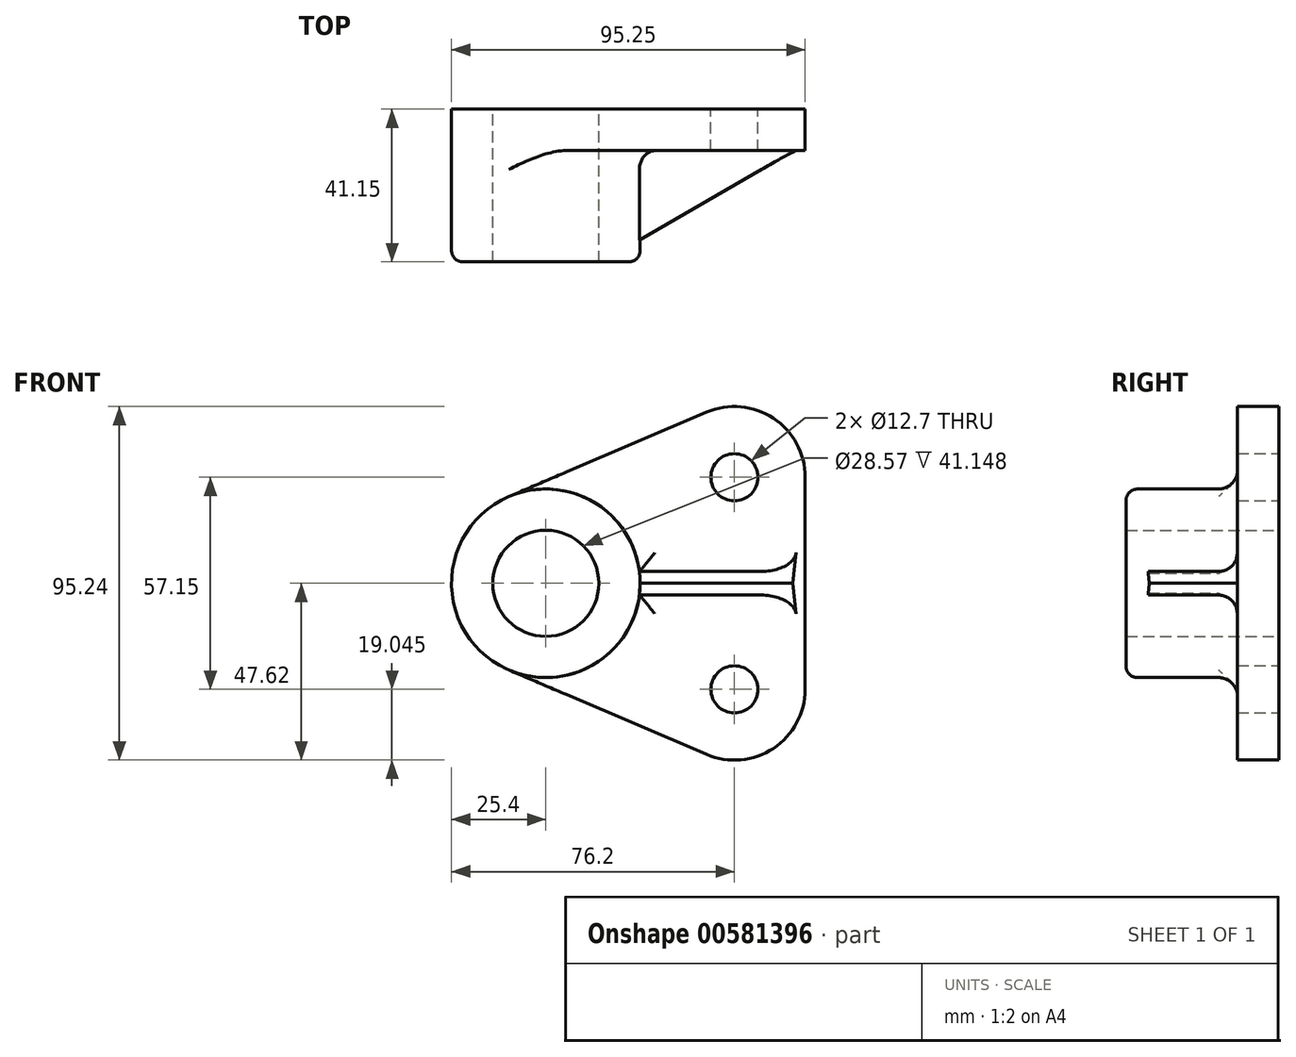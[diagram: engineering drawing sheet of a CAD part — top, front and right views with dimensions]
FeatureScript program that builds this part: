
annotation { "Feature Type Name" : "Feature", "Feature Type Description" : "" }
export const myFeature = defineFeature(function(context is Context, id is Id, definition is map)
    precondition{}
    {
        {
            var Q0;
            Q0=qCreatedBy(makeId("Front.planeOp"),FACE);
            var sketch = newSketch(context, id + "F0", { "sketchPlane" : qUnion([Q0])});
            skCircle(sketch, "E0", {"center": v(0, 0) * mm, "radius": 25.4 * mm});
            skCircle(sketch, "E1", {"center": v(0, 0) * mm, "radius": 14.29 * mm});
            skLineSegment(sketch, "E2", {"start": v(0, 0) * mm, "end": v(69.85, 0) * mm, "construction": true});
            skLineSegment(sketch, "E3", {"start": v(-9.97, 23.36) * mm, "end": v(43.33, 46.1) * mm});
            skLineSegment(sketch, "E4", {"start": v(69.85, 28.58) * mm, "end": v(69.85, 0) * mm});
            skPoint(sketch, "E5.visualSharp", {"position": v(69.85, 57.41) * mm});
            skArc(sketch, "E5.filletArc", {"start": v(69.85, 28.58) * mm, "mid": v(61.3, 44.47) * mm, "end": v(43.33, 46.1) * mm});
            skLineSegment(sketch, "E6.MirrorCS", {"start": v(69.85, -28.58) * mm, "end": v(69.85, 0) * mm});
            skArc(sketch, "E7.MirrorCS", {"start": v(69.85, -28.58) * mm, "mid": v(61.3, -44.47) * mm, "end": v(43.33, -46.1) * mm});
            skLineSegment(sketch, "E8.MirrorCS", {"start": v(-9.97, -23.36) * mm, "end": v(43.33, -46.1) * mm});
            skCircle(sketch, "E9", {"center": v(50.8, -28.58) * mm, "radius": 6.35 * mm});
            skCircle(sketch, "E10.MirrorC", {"center": v(50.8, 28.58) * mm, "radius": 6.35 * mm});
            skSolve(sketch);
        }
        {
            var Q0;
            Q0=makeQuery(id+"F0.imprint","IMPRINT",FACE,{"disambiguationData":[TD([[makeQuery(id+"F0.imprint","IMPRINT",EDGE,{"derivedFrom":sQuery(id+"F0.wireOp",EDGE,"E1")}),-1.0]])]});
            extrude(context, id + "F1", {"entities" : qUnion([Q0]), "depth" : 41.15 * mm, "offsetDistance" : 25.4 * mm});
        }
        {
            var Q0;
            Q0 = qSketchRegion(id + "F0", true);
            var Q1;
            Q1 = qSketchRegion(id + "F3", true);
            extrude(context, id + "F2", {"entities" : qUnion([Q0, Q1]), "operationType" : NewBodyOperationType.ADD, "depth" : 11.18 * mm, "offsetDistance" : 25.4 * mm});
        }
        {
            var Q0;
            Q0=qCreatedBy(makeId("Top.planeOp"),FACE);
            var sketch = newSketch(context, id + "F3", { "sketchPlane" : qUnion([Q0])});
            skLineSegment(sketch, "E11", {"start": v(25.4, -11.18) * mm, "end": v(25.4, -41.15) * mm});
            skLineSegment(sketch, "E12.0", {"start": v(69.85, -11.18) * mm, "end": v(43.33, -11.18) * mm});
            skLineSegment(sketch, "E13", {"start": v(66.55, -11.18) * mm, "end": v(25.4, -34.93) * mm});
            skLineSegment(sketch, "E14.0", {"start": v(-9.97, -11.18) * mm, "end": v(43.33, -11.18) * mm});
            skSolve(sketch);
        }
        {
            var Q0;
            {var subQ3=sQuery(id+"F3.wireOp",EDGE,"E13");Q0=makeQuery(id+"F3.imprint","IMPRINT",FACE,{"disambiguationData":[TD([[makeQuery(id+"F3.imprint","IMPRINT",EDGE,{"derivedFrom":subQ3}),-1.0]])]});}
            extrude(context, id + "F4", {"entities" : qUnion([Q0]), "operationType" : NewBodyOperationType.ADD, "endBound" : BoundingType.SYMMETRIC, "oppositeDirection" : true, "depth" : 6.35 * mm, "offsetDistance" : 25.4 * mm, "hasDraft" : true, "draftAngle" : 3 * degree});
        }
        {
            var Q0;
            Q0=makeQuery(id+"F1.opExtrude","CAP_EDGE",EDGE,{"disambiguationData":[OSD([sQuery(id+"F0.wireOp",EDGE,"E0")])],"isStart":false});
            fillet(context, id + "F5", {"entities" : qUnion([Q0]), "radius" : 3.05 * mm, "tangentPropagation" : true, "allowEdgeOverflow" : false});
        }
        {
            var Q0;
            {var subQ0=sQuery(id+"F0.wireOp",EDGE,"E0");var subQ1=makeQuery(id+"F1.opExtrude","SWEPT_FACE",FACE,{"disambiguationData":[OSD([subQ0])]});var subQ2=sQuery(id+"F0.wireOp",EDGE,"E8.MirrorCS");var subQ3=makeQuery(id+"F2.opExtrude","CAP_FACE",FACE,{"disambiguationData":[OSD([subQ0,sQuery(id+"F0.wireOp",EDGE,"E1"),sQuery(id+"F0.wireOp",EDGE,"E3"),sQuery(id+"F0.wireOp",EDGE,"E4"),sQuery(id+"F0.wireOp",EDGE,"E5.filletArc"),sQuery(id+"F0.wireOp",EDGE,"E6.MirrorCS"),sQuery(id+"F0.wireOp",EDGE,"E7.MirrorCS"),subQ2,sQuery(id+"F0.wireOp",EDGE,"E9"),sQuery(id+"F0.wireOp",EDGE,"E10.MirrorC")])],"isStart":false});Q0=makeQuery(id+"F4.boolean.opBoolean","SPLIT",EDGE,{"disambiguationData":[TD([makeQuery(id+"F2.opExtrude","SWEPT_FACE",FACE,{"disambiguationData":[OSD([subQ2])]})])],"derivedFrom":makeQuery(id+"F2.boolean.opBoolean","INTERSECT",EDGE,{"derivedFrom":[subQ1,subQ3]})});}
            var Q1;
            {var subQ0=sQuery(id+"F0.wireOp",EDGE,"E0");var subQ1=makeQuery(id+"F1.opExtrude","SWEPT_FACE",FACE,{"disambiguationData":[OSD([subQ0])]});var subQ2=sQuery(id+"F0.wireOp",EDGE,"E3");var subQ3=makeQuery(id+"F2.opExtrude","CAP_FACE",FACE,{"disambiguationData":[OSD([subQ0,sQuery(id+"F0.wireOp",EDGE,"E1"),subQ2,sQuery(id+"F0.wireOp",EDGE,"E4"),sQuery(id+"F0.wireOp",EDGE,"E5.filletArc"),sQuery(id+"F0.wireOp",EDGE,"E6.MirrorCS"),sQuery(id+"F0.wireOp",EDGE,"E7.MirrorCS"),sQuery(id+"F0.wireOp",EDGE,"E8.MirrorCS"),sQuery(id+"F0.wireOp",EDGE,"E9"),sQuery(id+"F0.wireOp",EDGE,"E10.MirrorC")])],"isStart":false});Q1=makeQuery(id+"F4.boolean.opBoolean","SPLIT",EDGE,{"disambiguationData":[TD([makeQuery(id+"F2.opExtrude","SWEPT_FACE",FACE,{"disambiguationData":[OSD([subQ2])]})])],"derivedFrom":makeQuery(id+"F2.boolean.opBoolean","INTERSECT",EDGE,{"derivedFrom":[subQ1,subQ3]})});}
            var Q2;
            Q2=makeQuery(id+"F4.boolean.opBoolean","INTERSECT",EDGE,{"derivedFrom":[makeQuery(id+"F2.opExtrude","CAP_FACE",FACE,{"disambiguationData":[OSD([sQuery(id+"F0.wireOp",EDGE,"E0"),sQuery(id+"F0.wireOp",EDGE,"E1"),sQuery(id+"F0.wireOp",EDGE,"E3"),sQuery(id+"F0.wireOp",EDGE,"E4"),sQuery(id+"F0.wireOp",EDGE,"E5.filletArc"),sQuery(id+"F0.wireOp",EDGE,"E6.MirrorCS"),sQuery(id+"F0.wireOp",EDGE,"E7.MirrorCS"),sQuery(id+"F0.wireOp",EDGE,"E8.MirrorCS"),sQuery(id+"F0.wireOp",EDGE,"E9"),sQuery(id+"F0.wireOp",EDGE,"E10.MirrorC")])],"isStart":false}),makeQuery(id+"F4.opExtrude","CAP_FACE",FACE,{"disambiguationData":[OSD([sQuery(id+"F3.wireOp",EDGE,"E12.0"),sQuery(id+"F3.wireOp",EDGE,"E11"),sQuery(id+"F3.wireOp",EDGE,"E13"),sQuery(id+"F3.wireOp",EDGE,"E14.0")])],"isStart":true})]});
            var Q3;
            Q3=makeQuery(id+"F4.boolean.opBoolean","INTERSECT",EDGE,{"derivedFrom":[makeQuery(id+"F2.opExtrude","CAP_FACE",FACE,{"disambiguationData":[OSD([sQuery(id+"F0.wireOp",EDGE,"E0"),sQuery(id+"F0.wireOp",EDGE,"E1"),sQuery(id+"F0.wireOp",EDGE,"E3"),sQuery(id+"F0.wireOp",EDGE,"E4"),sQuery(id+"F0.wireOp",EDGE,"E5.filletArc"),sQuery(id+"F0.wireOp",EDGE,"E6.MirrorCS"),sQuery(id+"F0.wireOp",EDGE,"E7.MirrorCS"),sQuery(id+"F0.wireOp",EDGE,"E8.MirrorCS"),sQuery(id+"F0.wireOp",EDGE,"E9"),sQuery(id+"F0.wireOp",EDGE,"E10.MirrorC")])],"isStart":false}),makeQuery(id+"F4.opExtrude","CAP_FACE",FACE,{"disambiguationData":[OSD([sQuery(id+"F3.wireOp",EDGE,"E12.0"),sQuery(id+"F3.wireOp",EDGE,"E11"),sQuery(id+"F3.wireOp",EDGE,"E13"),sQuery(id+"F3.wireOp",EDGE,"E14.0")])],"isStart":false})]});
            fillet(context, id + "F6", {"entities" : qUnion([Q0, Q1, Q2, Q3]), "radius" : 5.08 * mm, "allowEdgeOverflow" : false});
        }
    });
